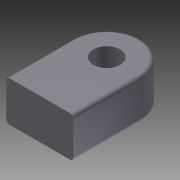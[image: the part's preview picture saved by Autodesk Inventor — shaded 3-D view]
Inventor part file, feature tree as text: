
AUTODESK INVENTOR PART (.ipt)
format: ipt  version: 2011 SP2 (Build 150309200, 309)  size: 101,888 bytes
history: native  units: mm
features: extrude x1, fillet x1, sketch x1
ambient origin geometry x8: Origin, YZ Plane, XZ Plane, XY Plane, X Axis, Y Axis, Z Axis, Center Point
bodies: Solid1 (feature_tree)
feature tree (3):
  extrude  "Extrusion1"  Depth=60.0mm
  fillet  "Fillet1"  Radius=8.0mm
  sketch  "Sketch1"  dims[d0=40.0mm d1=60.0mm d2=8.0mm d3=24.0mm d4=0.0mm d5=2.0mm]
